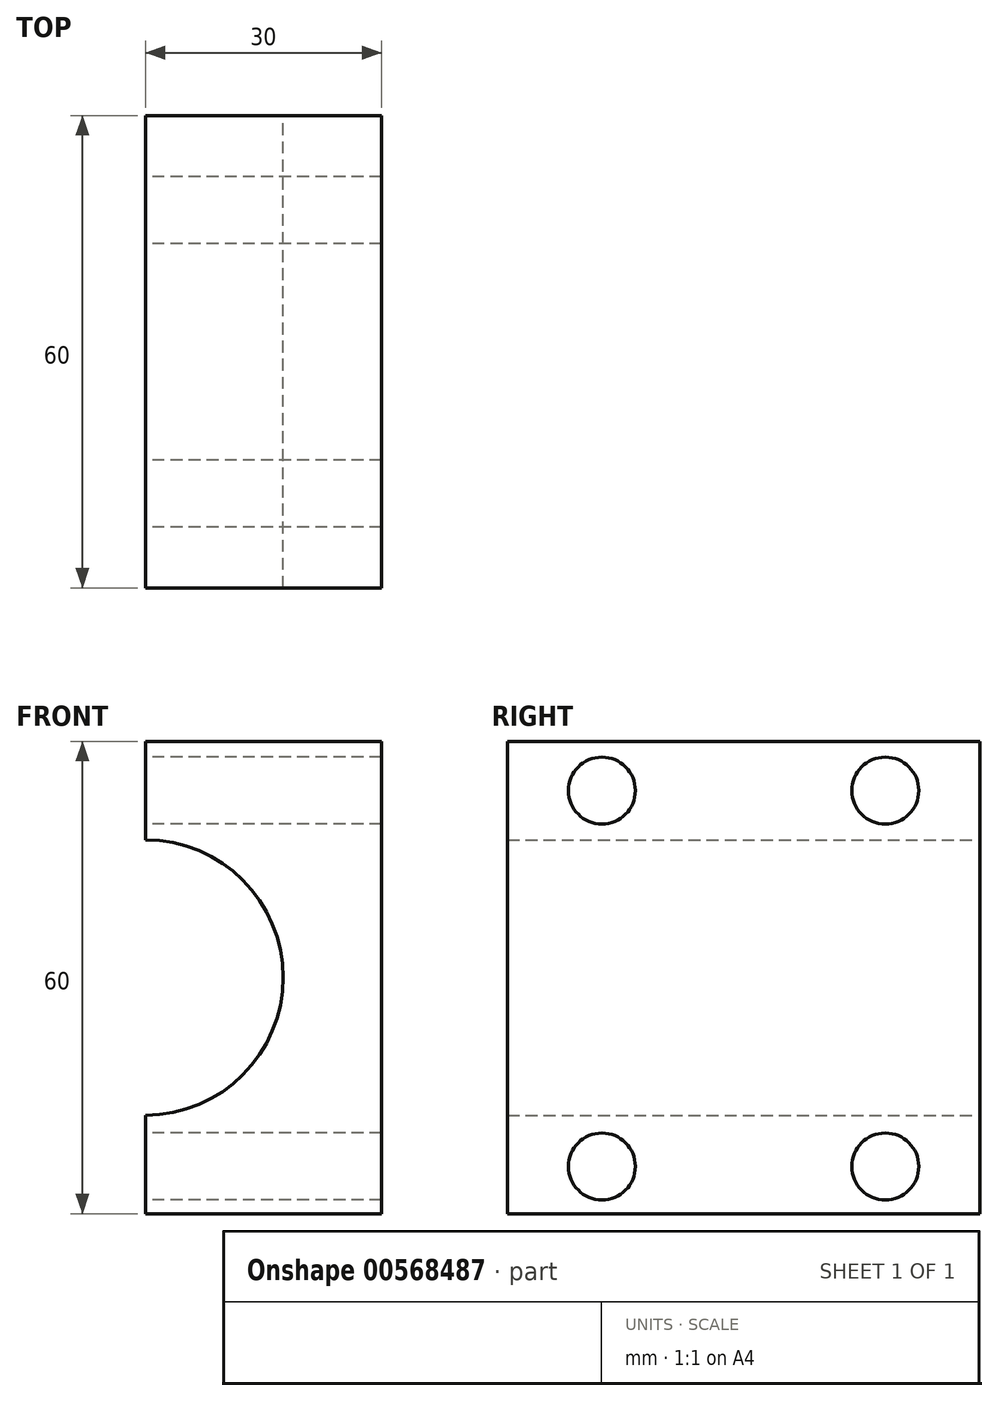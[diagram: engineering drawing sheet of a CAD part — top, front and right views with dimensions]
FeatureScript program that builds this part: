
annotation { "Feature Type Name" : "Feature", "Feature Type Description" : "" }
export const myFeature = defineFeature(function(context is Context, id is Id, definition is map)
    precondition{}
    {
        {
            var Q0;
            Q0=qCreatedBy(makeId("Front.planeOp"),FACE);
            var sketch = newSketch(context, id + "F0", { "sketchPlane" : qUnion([Q0])});
            skLineSegment(sketch, "E0.bottom", {"start": v(-15, -30) * mm, "end": v(15, -30) * mm});
            skLineSegment(sketch, "E0.top", {"start": v(-15, 30) * mm, "end": v(15, 30) * mm});
            skLineSegment(sketch, "E0.left", {"start": v(-15, -30) * mm, "end": v(-15, -17.5) * mm});
            skLineSegment(sketch, "E0.right", {"start": v(15, -30) * mm, "end": v(15, 30) * mm});
            skArc(sketch, "E1", {"start": v(-15, -17.5) * mm, "mid": v(2.5, 0) * mm, "end": v(-15, 17.5) * mm});
            skLineSegment(sketch, "E2.trimOffspring", {"start": v(-15, 17.5) * mm, "end": v(-15, 30) * mm});
            skSolve(sketch);
        }
        {
            var Q0;
            Q0=makeQuery(id+"F0.imprint","IMPRINT",FACE,{"disambiguationData":[TD([[makeQuery(id+"F0.imprint","IMPRINT",EDGE,{"derivedFrom":sQuery(id+"F0.wireOp",EDGE,"E0.bottom")}),1.0]])]});
            extrude(context, id + "F1", {"entities" : qUnion([Q0]), "endBound" : BoundingType.SYMMETRIC, "depth" : 60 * mm, "offsetDistance" : 25 * mm});
        }
        {
            var Q0;
            Q0=makeQuery(id+"F1.opExtrude","SWEPT_FACE",FACE,{"disambiguationData":[OSD([sQuery(id+"F0.wireOp",EDGE,"E2.trimOffspring")])]});
            var sketch = newSketch(context, id + "F2", { "sketchPlane" : qUnion([Q0])});
            skPoint(sketch, "E3", {"position": v(-18, 23.75) * mm});
            skLineSegment(sketch, "E4", {"start": v(-30, 23.75) * mm, "end": v(30, 23.75) * mm});
            skPoint(sketch, "E5", {"position": v(18, 23.75) * mm});
            skLineSegment(sketch, "E6", {"start": v(-29.94, -24) * mm, "end": v(29.86, -24) * mm});
            skLineSegment(sketch, "E7", {"start": v(18, 23.75) * mm, "end": v(18, -24) * mm, "construction": true});
            skLineSegment(sketch, "E8", {"start": v(-18, 23.75) * mm, "end": v(-18, -24) * mm, "construction": true});
            skPoint(sketch, "E9", {"position": v(-18, -24) * mm});
            skPoint(sketch, "E10", {"position": v(18, -24) * mm});
            skSolve(sketch);
        }
        {
            var Q0;
            Q0=sQuery(id+"F2.wireOp",VERTEX,"E5");
            var Q1;
            Q1=sQuery(id+"F2.wireOp",VERTEX,"E3");
            var Q2;
            Q2=sQuery(id+"F2.wireOp",VERTEX,"E9");
            var Q3;
            Q3=sQuery(id+"F2.wireOp",VERTEX,"E10");
            var Q4;
            Q4=makeQuery(id+"F1.opExtrude","SWEPT_BODY",BODY,{"disambiguationData":[OSD([sQuery(id+"F0.wireOp",EDGE,"E0.bottom"),sQuery(id+"F0.wireOp",EDGE,"E0.top"),sQuery(id+"F0.wireOp",EDGE,"E0.left"),sQuery(id+"F0.wireOp",EDGE,"E0.right"),sQuery(id+"F0.wireOp",EDGE,"E1"),sQuery(id+"F0.wireOp",EDGE,"E2.trimOffspring")])]});
            hole(context, id + "F3", {"style" : HoleStyle.SIMPLE, "endStyle" : HoleEndStyle.THROUGH, "holeDiameter" : 8.5 * mm, "isTappedThrough" : true, "tappedDepth" : 12 * mm, "tapClearance" : 3, "locations" : qUnion([Q0, Q1, Q2, Q3]), "scope" : qUnion([Q4]), "majorDiameter" : 5 * mm});
        }
    });
